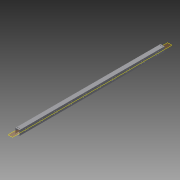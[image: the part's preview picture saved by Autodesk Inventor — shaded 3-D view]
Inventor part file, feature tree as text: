
AUTODESK INVENTOR PART (.ipt)
format: ipt  version: 2015 SP1 (Build 190203100, 203)  size: 193,536 bytes
history: native  units: in
note: dims shown in document units (in); Inventor stores cm internally (conversion verified against a paired STEP export)
features: extrude x3, sketch x2
ambient origin geometry x8: Origin, YZ Plane, XZ Plane, XY Plane, X Axis, Y Axis, Z Axis, Center Point
bodies: Solid1 (feature_tree)
feature tree (5):
  extrude  "Extrusion1"  Depth=1.9685in
  extrude  "Extrusion2"  Depth=56.2992in TaperAngle=0.0deg
  extrude  "Extrusion3"  Depth=0.0787in
  sketch  "Sketch3"  dims[d0=1.5748in d1=1.9685in]
  sketch  "Sketch4"  dims[d3=0.0787in d4=56.2992in d5=0.0in d6=0.0787in d7=0.0787in d8=0.0787in d9=0.2756in d10=0.9843in d11=0.7874in d13=2.3228in d14=3.937in d16=5.6299in d17=0.3937in d19=0.3937in d21=0.3937in d22=0.0in d23=0.2756in d24=0.4921in d25=0.7087in d26=0.4921in d27=0.0in d28=0.0in]
